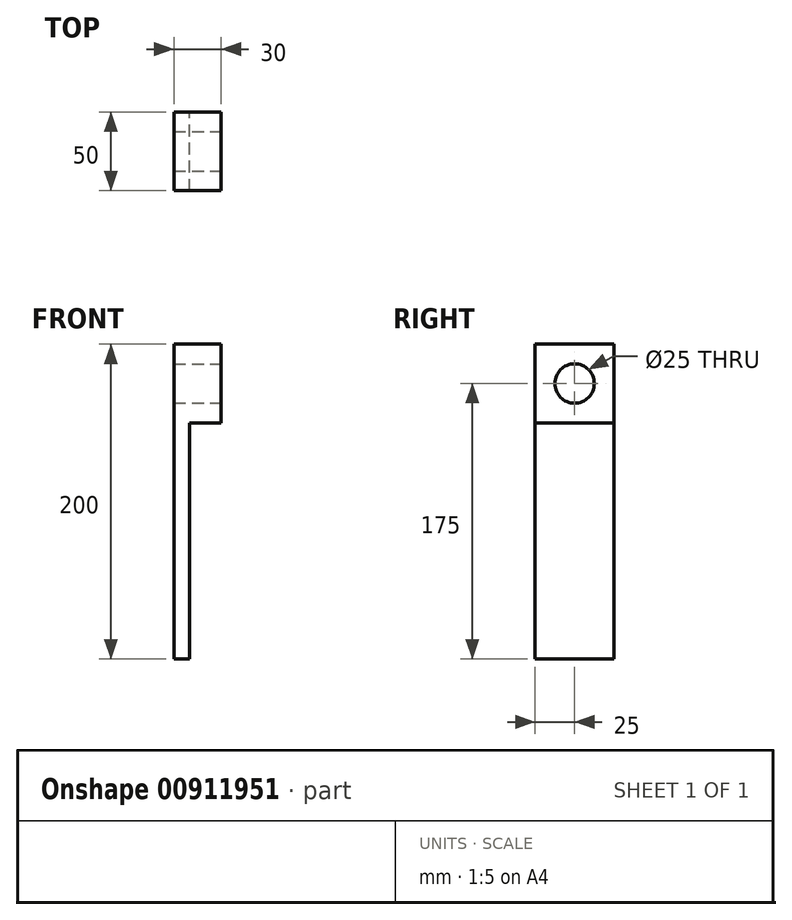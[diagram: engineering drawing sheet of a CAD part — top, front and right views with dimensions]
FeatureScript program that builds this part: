
annotation { "Feature Type Name" : "Feature", "Feature Type Description" : "" }
export const myFeature = defineFeature(function(context is Context, id is Id, definition is map)
    precondition{}
    {
        {
            var Q0;
            Q0=qCreatedBy(makeId("Front.planeOp"),FACE);
            var sketch = newSketch(context, id + "F0", { "sketchPlane" : qUnion([Q0])});
            skLineSegment(sketch, "E0", {"start": v(0, 0) * mm, "end": v(0, 200) * mm});
            skLineSegment(sketch, "E1", {"start": v(0, 200) * mm, "end": v(30, 200) * mm});
            skLineSegment(sketch, "E2", {"start": v(30, 200) * mm, "end": v(30, 150) * mm});
            skLineSegment(sketch, "E3", {"start": v(30, 150) * mm, "end": v(10, 150) * mm});
            skLineSegment(sketch, "E4", {"start": v(10, 150) * mm, "end": v(10, 0) * mm});
            skLineSegment(sketch, "E5", {"start": v(10, 0) * mm, "end": v(0, 0) * mm});
            skSolve(sketch);
        }
        {
            var Q0;
            Q0 = qSketchRegion(id + "F0", true);
            extrude(context, id + "F1", {"entities" : qUnion([Q0]), "depth" : 50 * mm, "offsetDistance" : 25 * mm});
        }
        {
            var Q0;
            Q0=makeQuery(id+"F1.opExtrude","SWEPT_FACE",FACE,{"disambiguationData":[OSD([sQuery(id+"F0.wireOp",EDGE,"E2")])]});
            var sketch = newSketch(context, id + "F2", { "sketchPlane" : qUnion([Q0])});
            skCircle(sketch, "E6", {"center": v(-25, 175) * mm, "radius": 12.5 * mm});
            skPoint(sketch, "E6.centerSnap0", {"position": v(-25, 200) * mm});
            skSolve(sketch);
        }
        {
            var Q0;
            Q0 = qSketchRegion(id + "F2", true);
            extrude(context, id + "F3", {"entities" : qUnion([Q0]), "operationType" : NewBodyOperationType.REMOVE, "oppositeDirection" : true, "depth" : 56 * mm, "offsetDistance" : 25 * mm});
        }
    });
